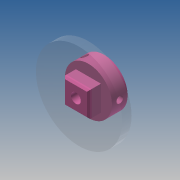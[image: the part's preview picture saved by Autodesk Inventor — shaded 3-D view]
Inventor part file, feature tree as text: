
AUTODESK INVENTOR PART (.ipt)
format: ipt  version: 2017 (Build 210142000, 142)  size: 242,688 bytes
history: native  units: mm
features: extrude x5, sketch x3, other x2, chamfer x2, pattern_circular x1, projected_geometry x1
ambient origin geometry x8: Origin, YZ Plane, XZ Plane, XY Plane, X Axis, Y Axis, Z Axis, Center Point
bodies: Body1 (feature_tree), Body2 (feature_tree)
feature tree (14):
  other  "Sólido1"
  extrude  "Extrusión1"  Depth=11.85mm
  sketch  "Boceto2"  dims[d3=6.576542mm d4=3.3mm]
  extrude  "Extrusión2"  Depth=3.3mm
  extrude  "Extrusión3"  Depth=2.0mm
  sketch  "Boceto3"  dims[d5=10.0mm d6=0.0mm d7=4.2mm d8=120.0deg d9=3.7mm d10=16.0mm d11=0.0mm d12=4.0mm d13=0.0mm d14=8.0mm d15=0.0mm d16=30.0mm d18=360.0deg d20=30.0mm d21=360.0deg d23=1.0mm d24=2.0mm d25=45.0deg d26=30.0mm d27=4.275mm d28=4.275mm d32=16.0mm d33=55.0mm d34=6.0mm d35=0.0mm d36=1.0mm d37=2.0mm d38=45.0deg]
  extrude  "Extrusión4"  TaperAngle=120.0deg  [1 undecoded]
  pattern_circular  "Patrón circular1"  [2 undecoded]
  chamfer  "Chaflán1"  Distance=16.0mm
  extrude  "Extrusión5"  Depth=2.0mm TaperAngle=0.0deg
  chamfer  "Chaflán3"  Distance=8.0mm
  sketch  "Boceto1"  dims[d0=6.3mm d2=11.85mm]
  projected_geometry  "Contorno proyectado1"
  other  "Sólido2"
note: 3 required parameter values undecoded (feature->parameter linkage not recoverable at this tier; creation-order binding heuristic only, values carry confidence <= 0.55)
